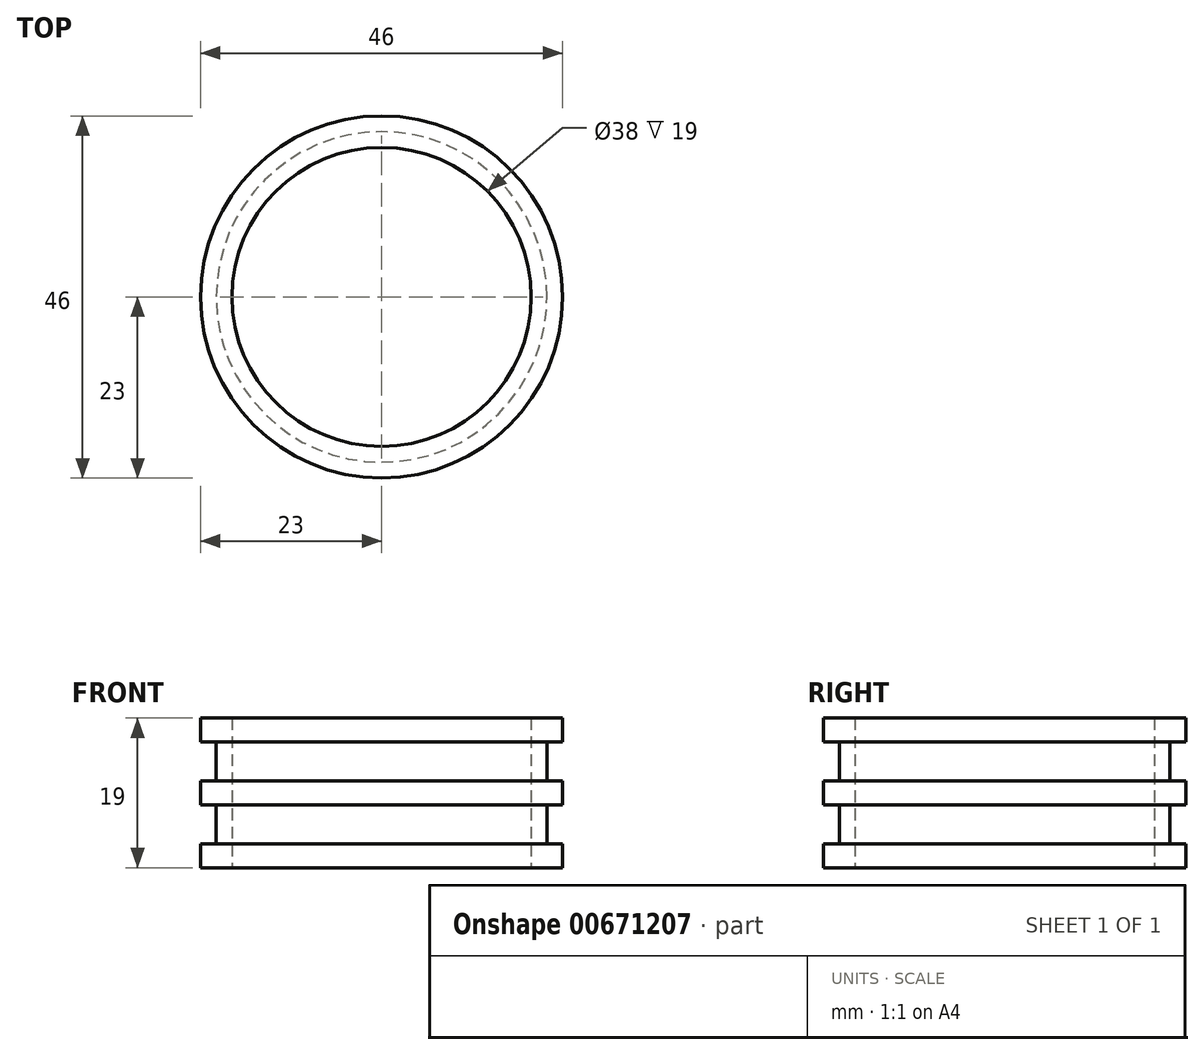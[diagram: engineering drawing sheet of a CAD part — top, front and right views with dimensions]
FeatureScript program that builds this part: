
annotation { "Feature Type Name" : "Feature", "Feature Type Description" : "" }
export const myFeature = defineFeature(function(context is Context, id is Id, definition is map)
    precondition{}
    {
        {
            var Q0;
            Q0=qCreatedBy(makeId("Front.planeOp"),FACE);
            var sketch = newSketch(context, id + "F0", { "sketchPlane" : qUnion([Q0])});
            skLineSegment(sketch, "E0", {"start": v(0, 26.94) * mm, "end": v(23, 26.94) * mm});
            skLineSegment(sketch, "E1", {"start": v(23, 26.94) * mm, "end": v(23, 23.94) * mm});
            skLineSegment(sketch, "E2", {"start": v(23, 23.94) * mm, "end": v(21, 23.94) * mm});
            skLineSegment(sketch, "E3", {"start": v(21, 23.94) * mm, "end": v(21, 18.94) * mm});
            skLineSegment(sketch, "E4", {"start": v(21, 18.94) * mm, "end": v(23, 18.94) * mm});
            skLineSegment(sketch, "E5", {"start": v(23, 18.94) * mm, "end": v(23, 15.94) * mm});
            skLineSegment(sketch, "E6", {"start": v(23, 15.94) * mm, "end": v(21, 15.94) * mm});
            skLineSegment(sketch, "E7", {"start": v(21, 15.94) * mm, "end": v(21, 10.94) * mm});
            skLineSegment(sketch, "E8", {"start": v(21, 10.94) * mm, "end": v(23, 10.94) * mm});
            skLineSegment(sketch, "E9", {"start": v(23, 10.94) * mm, "end": v(23, 7.94) * mm});
            skLineSegment(sketch, "E10", {"start": v(23, 7.94) * mm, "end": v(0, 7.94) * mm});
            skLineSegment(sketch, "E11", {"start": v(0, 26.94) * mm, "end": v(0, 7.94) * mm});
            skSolve(sketch);
        }
        {
            var Q0;
            Q0=makeQuery(id+"F0.imprint","IMPRINT",FACE,{"disambiguationData":[TD([[makeQuery(id+"F0.imprint","IMPRINT",EDGE,{"derivedFrom":sQuery(id+"F0.wireOp",EDGE,"E0")}),-1.0]])]});
            var Q1;
            Q1=sQuery(id+"F0.wireOp",EDGE,"E11");
            revolve(context, id + "F1", {"entities" : qUnion([Q0]), "axis" : qUnion([Q1]), "revolveType" : RevolveType.FULL});
        }
        {
            var Q0;
            Q0=makeQuery(id+"F1.opRevolve","SWEPT_FACE",FACE,{"disambiguationData":[OSD([sQuery(id+"F0.wireOp",EDGE,"E10")])]});
            var sketch = newSketch(context, id + "F2", { "sketchPlane" : qUnion([Q0])});
            skPoint(sketch, "E12", {"position": v(0, 0) * mm});
            skSolve(sketch);
        }
        {
            var Q0;
            Q0=makeQuery(id+"F2.imprint","IMPRINT",FACE,{"disambiguationData":[TD([[makeQuery(id+"F2.imprint","IMPRINT",EDGE,{"derivedFrom":makeQuery(id+"F1.opRevolve","SWEPT_EDGE",EDGE,{"disambiguationData":[OSD([sQuery(id+"F0.wireOp",EDGE,"E9"),sQuery(id+"F0.wireOp",EDGE,"E10")])]})}),-1.0]])]});
            var sketch = newSketch(context, id + "F3", { "sketchPlane" : qUnion([Q0])});
            skCircle(sketch, "E13", {"center": v(0, 0) * mm, "radius": 19 * mm});
            skSolve(sketch);
        }
        {
            var Q0;
            Q0=makeQuery(id+"F3.imprint","IMPRINT",FACE,{"disambiguationData":[TD([[makeQuery(id+"F3.imprint","IMPRINT",EDGE,{"derivedFrom":sQuery(id+"F3.wireOp",EDGE,"E13")}),1.0]])]});
            extrude(context, id + "F4", {"entities" : qUnion([Q0]), "operationType" : NewBodyOperationType.REMOVE, "oppositeDirection" : true, "depth" : 23 * mm, "offsetDistance" : 25 * mm});
        }
    });
